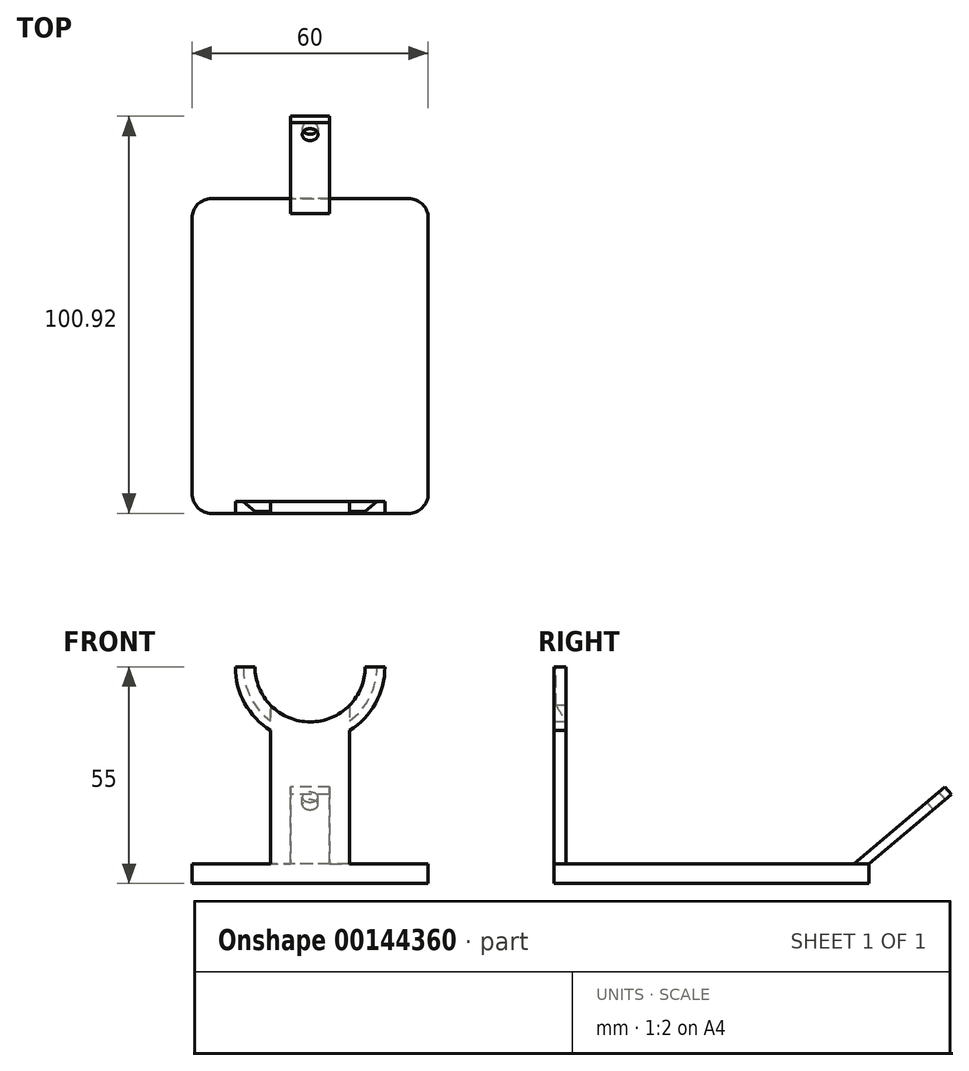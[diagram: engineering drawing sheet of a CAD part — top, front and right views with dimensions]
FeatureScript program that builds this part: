
annotation { "Feature Type Name" : "Feature", "Feature Type Description" : "" }
export const myFeature = defineFeature(function(context is Context, id is Id, definition is map)
    precondition{}
    {
        {
            var Q0;
            Q0=qCreatedBy(makeId("Top.planeOp"),FACE);
            var sketch = newSketch(context, id + "F0", { "sketchPlane" : qUnion([Q0])});
            skLineSegment(sketch, "E0.bottom", {"start": v(-25, 40) * mm, "end": v(25, 40) * mm});
            skLineSegment(sketch, "E0.top", {"start": v(-25, -40) * mm, "end": v(25, -40) * mm});
            skLineSegment(sketch, "E0.left", {"start": v(-30, 35) * mm, "end": v(-30, -35) * mm});
            skLineSegment(sketch, "E0.right", {"start": v(30, 35) * mm, "end": v(30, -35) * mm});
            skPoint(sketch, "E1.visualSharp", {"position": v(-30, 40) * mm});
            skArc(sketch, "E1.filletArc", {"start": v(-25, 40) * mm, "mid": v(-28.54, 38.54) * mm, "end": v(-30, 35) * mm});
            skPoint(sketch, "E2.visualSharp", {"position": v(30, 40) * mm});
            skArc(sketch, "E2.filletArc", {"start": v(30, 35) * mm, "mid": v(28.54, 38.54) * mm, "end": v(25, 40) * mm});
            skPoint(sketch, "E3.visualSharp", {"position": v(30, -40) * mm});
            skArc(sketch, "E3.filletArc", {"start": v(25, -40) * mm, "mid": v(28.54, -38.54) * mm, "end": v(30, -35) * mm});
            skPoint(sketch, "E4.visualSharp", {"position": v(-30, -40) * mm});
            skArc(sketch, "E4.filletArc", {"start": v(-30, -35) * mm, "mid": v(-28.54, -38.54) * mm, "end": v(-25, -40) * mm});
            skSolve(sketch);
        }
        {
            var Q0;
            Q0 = qSketchRegion(id + "F0", true);
            extrude(context, id + "F1", {"entities" : qUnion([Q0]), "depth" : 5 * mm});
        }
        {
            var Q0;
            Q0=qCreatedBy(makeId("Right.planeOp"),FACE);
            var sketch = newSketch(context, id + "F2", { "sketchPlane" : qUnion([Q0])});
            skLineSegment(sketch, "E5", {"start": v(40, 5) * mm, "end": v(60.92, 22.56) * mm});
            skLineSegment(sketch, "E6", {"start": v(60.92, 22.56) * mm, "end": v(59.31, 24.47) * mm});
            skLineSegment(sketch, "E7", {"start": v(59.31, 24.47) * mm, "end": v(36.11, 5) * mm});
            skLineSegment(sketch, "E8", {"start": v(40, 5) * mm, "end": v(36.11, 5) * mm});
            skSolve(sketch);
        }
        {
            var Q0;
            Q0 = qSketchRegion(id + "F2", true);
            extrude(context, id + "F3", {"entities" : qUnion([Q0]), "operationType" : NewBodyOperationType.ADD, "endBound" : BoundingType.SYMMETRIC, "depth" : 10 * mm});
        }
        {
            var Q0;
            Q0=qCreatedBy(makeId("Right.planeOp"),FACE);
            var sketch = newSketch(context, id + "F4", { "sketchPlane" : qUnion([Q0])});
            skLineSegment(sketch, "E9.bottom", {"start": v(-40, 55) * mm, "end": v(-37, 55) * mm});
            skLineSegment(sketch, "E9.top", {"start": v(-40, 5) * mm, "end": v(-37, 5) * mm});
            skLineSegment(sketch, "E9.left", {"start": v(-40, 55) * mm, "end": v(-40, 5) * mm});
            skLineSegment(sketch, "E9.right", {"start": v(-37, 55) * mm, "end": v(-37, 5) * mm});
            skSolve(sketch);
        }
        {
            var Q0;
            Q0 = qSketchRegion(id + "F4", true);
            extrude(context, id + "F5", {"entities" : qUnion([Q0]), "operationType" : NewBodyOperationType.ADD, "endBound" : BoundingType.SYMMETRIC, "depth" : 20 * mm});
        }
        {
            var Q0;
            Q0=makeQuery(id+"F5.boolean.opBoolean","MERGE",FACE,{"derivedFrom":[makeQuery(id+"F1.opExtrude","SWEPT_FACE",FACE,{"disambiguationData":[OSD([sQuery(id+"F0.wireOp",EDGE,"E0.top")])]}),makeQuery(id+"F5.opExtrude","SWEPT_FACE",FACE,{"disambiguationData":[OSD([sQuery(id+"F4.wireOp",EDGE,"E9.left")])]})]});
            var sketch = newSketch(context, id + "F6", { "sketchPlane" : qUnion([Q0])});
            skArc(sketch, "E10", {"start": v(-14, 55) * mm, "mid": v(0, 41) * mm, "end": v(14, 55) * mm});
            skArc(sketch, "E11.0", {"start": v(-19, 55) * mm, "mid": v(0, 36) * mm, "end": v(19, 55) * mm});
            skLineSegment(sketch, "E12", {"start": v(-19, 55) * mm, "end": v(-14, 55) * mm});
            skLineSegment(sketch, "E13", {"start": v(14, 55) * mm, "end": v(19, 55) * mm});
            skSolve(sketch);
        }
        {
            var Q0;
            Q0 = qSketchRegion(id + "F6", true);
            extrude(context, id + "F7", {"entities" : qUnion([Q0]), "operationType" : NewBodyOperationType.ADD, "oppositeDirection" : true, "depth" : 3 * mm});
        }
        {
            var Q0;
            Q0=makeQuery(id+"F7.boolean.opBoolean","MERGE",FACE,{"derivedFrom":[makeQuery(id+"F5.boolean.opBoolean","MERGE",FACE,{"derivedFrom":[makeQuery(id+"F1.opExtrude","SWEPT_FACE",FACE,{"disambiguationData":[OSD([sQuery(id+"F0.wireOp",EDGE,"E0.top")])]}),makeQuery(id+"F5.opExtrude","SWEPT_FACE",FACE,{"disambiguationData":[OSD([sQuery(id+"F4.wireOp",EDGE,"E9.left")])]})]}),makeQuery(id+"F7.opExtrude","CAP_FACE",FACE,{"disambiguationData":[OSD([sQuery(id+"F6.wireOp",EDGE,"E10"),sQuery(id+"F6.wireOp",EDGE,"E11.0"),sQuery(id+"F6.wireOp",EDGE,"E12"),sQuery(id+"F6.wireOp",EDGE,"E13")])],"isStart":true})]});
            var sketch = newSketch(context, id + "F8", { "sketchPlane" : qUnion([Q0])});
            skArc(sketch, "E14", {"start": v(-14, 55) * mm, "mid": v(0, 41.02) * mm, "end": v(14, 55) * mm});
            skLineSegment(sketch, "E15", {"start": v(-14, 55) * mm, "end": v(14, 55) * mm});
            skSolve(sketch);
        }
        {
            var Q0;
            Q0 = qSketchRegion(id + "F8", true);
            extrude(context, id + "F9", {"entities" : qUnion([Q0]), "operationType" : NewBodyOperationType.REMOVE, "endBound" : BoundingType.THROUGH_ALL, "oppositeDirection" : true, "depth" : 25 * mm});
        }
        {
            var Q0;
            {var subQ0=sQuery(id+"F6.wireOp",EDGE,"E13");var subQ1=sQuery(id+"F6.wireOp",EDGE,"E12");var subQ2=sQuery(id+"F6.wireOp",EDGE,"E10");var subQ10=makeQuery(id+"F7.opExtrude","CAP_EDGE",EDGE,{"disambiguationData":[OSD([subQ2])],"isStart":false});Q0=makeQuery(id+"F9.boolean.opBoolean","MERGE",EDGE,{"derivedFrom":[makeQuery(id+"F7.boolean.opBoolean","SPLIT",EDGE,{"disambiguationData":[TD([makeQuery(id+"F7.opExtrude","SWEPT_FACE",FACE,{"disambiguationData":[OSD([subQ1])]})])],"derivedFrom":subQ10}),makeQuery(id+"F7.boolean.opBoolean","SPLIT",EDGE,{"disambiguationData":[TD([makeQuery(id+"F7.opExtrude","SWEPT_FACE",FACE,{"disambiguationData":[OSD([subQ0])]})])],"derivedFrom":subQ10})]});}
            chamfer(context, id + "F10", {"entities" : qUnion([Q0]), "chamferType" : ChamferType.OFFSET_ANGLE, "width" : 3 * mm, "oppositeDirection" : false, "angle" : 40 * degree, "tangentPropagation" : true});
        }
        {
            var Q0;
            Q0=makeQuery(id+"F3.opExtrude","SWEPT_FACE",FACE,{"disambiguationData":[OSD([sQuery(id+"F2.wireOp",EDGE,"E7")])]});
            var sketch = newSketch(context, id + "F11", { "sketchPlane" : qUnion([Q0])});
            skCircle(sketch, "E16", {"center": v(0, 57.17) * mm, "radius": 2 * mm});
            skSolve(sketch);
        }
        {
            var Q0;
            Q0 = qSketchRegion(id + "F11", true);
            extrude(context, id + "F12", {"entities" : qUnion([Q0]), "operationType" : NewBodyOperationType.REMOVE, "endBound" : BoundingType.THROUGH_ALL, "oppositeDirection" : true, "depth" : 25 * mm});
        }
    });
